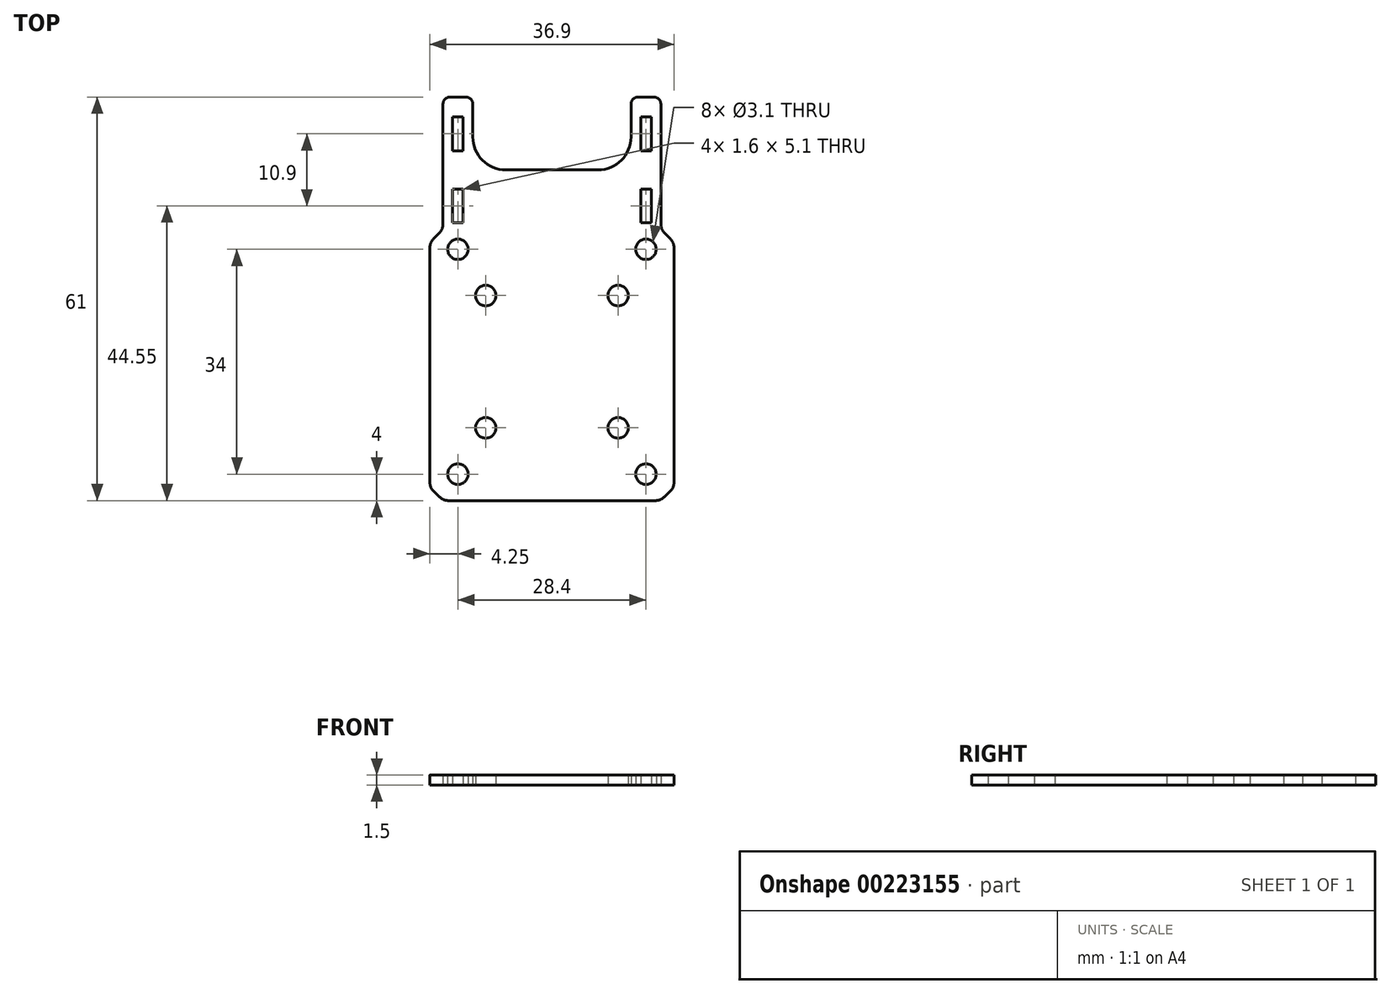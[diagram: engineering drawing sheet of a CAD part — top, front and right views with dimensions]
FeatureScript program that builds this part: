
annotation { "Feature Type Name" : "Feature", "Feature Type Description" : "" }
export const myFeature = defineFeature(function(context is Context, id is Id, definition is map)
    precondition{}
    {
        {
            var Q0;
            Q0=qCreatedBy(makeId("Top.planeOp"),FACE);
            var sketch = newSketch(context, id + "F0", { "sketchPlane" : qUnion([Q0])});
            skLineSegment(sketch, "E0.bottom", {"start": v(16.45, -30.5) * mm, "end": v(-16.45, -30.5) * mm});
            skLineSegment(sketch, "E0.left", {"start": v(16.45, -30.5) * mm, "end": v(16.45, 30.5) * mm});
            skLineSegment(sketch, "E0.right", {"start": v(-16.45, -30.5) * mm, "end": v(-16.45, 30.5) * mm});
            skPoint(sketch, "E0.middle", {"position": v(0, 0) * mm});
            skLineSegment(sketch, "E1.bottom", {"start": v(-15, 27.5) * mm, "end": v(-13.4, 27.5) * mm});
            skLineSegment(sketch, "E1.top", {"start": v(-15, 22.4) * mm, "end": v(-13.4, 22.4) * mm});
            skLineSegment(sketch, "E1.left", {"start": v(-15, 27.5) * mm, "end": v(-15, 22.4) * mm});
            skLineSegment(sketch, "E1.right", {"start": v(-13.4, 27.5) * mm, "end": v(-13.4, 22.4) * mm});
            skLineSegment(sketch, "E2.bottom", {"start": v(15, 27.5) * mm, "end": v(13.4, 27.5) * mm});
            skLineSegment(sketch, "E2.top", {"start": v(15, 22.4) * mm, "end": v(13.4, 22.4) * mm});
            skLineSegment(sketch, "E2.left", {"start": v(15, 27.5) * mm, "end": v(15, 22.4) * mm});
            skLineSegment(sketch, "E2.right", {"start": v(13.4, 27.5) * mm, "end": v(13.4, 22.4) * mm});
            skLineSegment(sketch, "E3.bottom", {"start": v(-15, 16.6) * mm, "end": v(-13.4, 16.6) * mm});
            skLineSegment(sketch, "E3.top", {"start": v(-15, 11.5) * mm, "end": v(-13.4, 11.5) * mm});
            skLineSegment(sketch, "E3.left", {"start": v(-15, 16.6) * mm, "end": v(-15, 11.5) * mm});
            skLineSegment(sketch, "E3.right", {"start": v(-13.4, 16.6) * mm, "end": v(-13.4, 11.5) * mm});
            skLineSegment(sketch, "E4.bottom", {"start": v(13.4, 16.6) * mm, "end": v(15, 16.6) * mm});
            skLineSegment(sketch, "E4.top", {"start": v(13.4, 11.5) * mm, "end": v(15, 11.5) * mm});
            skLineSegment(sketch, "E4.left", {"start": v(13.4, 16.6) * mm, "end": v(13.4, 11.5) * mm});
            skLineSegment(sketch, "E4.right", {"start": v(15, 16.6) * mm, "end": v(15, 11.5) * mm});
            skCircle(sketch, "E5", {"center": v(-10, 0.5) * mm, "radius": 1.55 * mm});
            skCircle(sketch, "E6", {"center": v(10, 0.5) * mm, "radius": 1.55 * mm});
            skCircle(sketch, "E7", {"center": v(10, -19.5) * mm, "radius": 1.55 * mm});
            skCircle(sketch, "E8", {"center": v(-10, -19.5) * mm, "radius": 1.55 * mm});
            skCircle(sketch, "E9", {"center": v(14.2, 7.5) * mm, "radius": 1.55 * mm});
            skPoint(sketch, "E9.centerSnap0", {"position": v(14.2, 11.5) * mm});
            skCircle(sketch, "E10", {"center": v(-14.2, 7.5) * mm, "radius": 1.55 * mm});
            skPoint(sketch, "E10.centerSnap0", {"position": v(-14.2, 11.5) * mm});
            skLineSegment(sketch, "E11", {"start": v(-16.45, 30.5) * mm, "end": v(-11.95, 30.5) * mm});
            skLineSegment(sketch, "E12", {"start": v(-11.95, 30.5) * mm, "end": v(-11.95, 19.5) * mm});
            skLineSegment(sketch, "E13", {"start": v(-11.95, 19.5) * mm, "end": v(11.95, 19.5) * mm});
            skLineSegment(sketch, "E14", {"start": v(11.95, 19.5) * mm, "end": v(11.95, 30.5) * mm});
            skLineSegment(sketch, "E15", {"start": v(11.95, 30.5) * mm, "end": v(16.45, 30.5) * mm});
            skCircle(sketch, "E16", {"center": v(14.2, -26.5) * mm, "radius": 1.55 * mm});
            skCircle(sketch, "E17", {"center": v(-14.2, -26.5) * mm, "radius": 1.55 * mm});
            skLineSegment(sketch, "E18.bottom", {"start": v(16.45, 10.5) * mm, "end": v(18.45, 8.5) * mm});
            skLineSegment(sketch, "E18.top", {"start": v(16.45, -30.5) * mm, "end": v(18.45, -28.5) * mm});
            skLineSegment(sketch, "E18.left", {"start": v(16.45, 10.5) * mm, "end": v(16.45, -30.5) * mm});
            skLineSegment(sketch, "E18.right", {"start": v(18.45, 8.5) * mm, "end": v(18.45, -28.5) * mm});
            skLineSegment(sketch, "E19.bottom", {"start": v(-16.45, 10.5) * mm, "end": v(-18.45, 8.5) * mm});
            skLineSegment(sketch, "E19.top", {"start": v(-16.45, -30.5) * mm, "end": v(-18.45, -28.5) * mm});
            skLineSegment(sketch, "E19.left", {"start": v(-16.45, 10.5) * mm, "end": v(-16.45, -30.5) * mm});
            skLineSegment(sketch, "E19.right", {"start": v(-18.45, 8.5) * mm, "end": v(-18.45, -28.5) * mm});
            skSolve(sketch);
        }
        {
            var Q0;
            Q0 = qSketchRegion(id + "F0", true);
            extrude(context, id + "F1", {"entities" : qUnion([Q0]), "depth" : 1.5 * mm});
        }
        {
            var Q0;
            Q0=makeQuery(id+"F1.opExtrude","SWEPT_EDGE",EDGE,{"disambiguationData":[OSD([sQuery(id+"F0.wireOp",EDGE,"E12"),sQuery(id+"F0.wireOp",EDGE,"E13")])]});
            var Q1;
            Q1=makeQuery(id+"F1.opExtrude","SWEPT_EDGE",EDGE,{"disambiguationData":[OSD([sQuery(id+"F0.wireOp",EDGE,"E13"),sQuery(id+"F0.wireOp",EDGE,"E14")])]});
            fillet(context, id + "F2", {"entities" : qUnion([Q0, Q1]), "radius" : 5 * mm, "tangentPropagation" : true, "allowEdgeOverflow" : false});
        }
        {
            var Q0;
            Q0=makeQuery(id+"F1.opExtrude","SWEPT_EDGE",EDGE,{"disambiguationData":[OSD([sQuery(id+"F0.wireOp",EDGE,"E0.left"),sQuery(id+"F0.wireOp",EDGE,"E18.top"),sQuery(id+"F0.wireOp",EDGE,"E18.left")])]});
            var Q1;
            Q1=makeQuery(id+"F1.opExtrude","SWEPT_EDGE",EDGE,{"disambiguationData":[OSD([sQuery(id+"F0.wireOp",EDGE,"E18.top"),sQuery(id+"F0.wireOp",EDGE,"E18.right")])]});
            var Q2;
            Q2=makeQuery(id+"F1.opExtrude","SWEPT_EDGE",EDGE,{"disambiguationData":[OSD([sQuery(id+"F0.wireOp",EDGE,"E19.top"),sQuery(id+"F0.wireOp",EDGE,"E19.right")])]});
            var Q3;
            Q3=makeQuery(id+"F1.opExtrude","SWEPT_EDGE",EDGE,{"disambiguationData":[OSD([sQuery(id+"F0.wireOp",EDGE,"E0.right"),sQuery(id+"F0.wireOp",EDGE,"E19.top"),sQuery(id+"F0.wireOp",EDGE,"E19.left")])]});
            var Q4;
            Q4=makeQuery(id+"F1.opExtrude","SWEPT_EDGE",EDGE,{"disambiguationData":[OSD([sQuery(id+"F0.wireOp",EDGE,"E19.bottom"),sQuery(id+"F0.wireOp",EDGE,"E19.right")])]});
            var Q5;
            Q5=makeQuery(id+"F1.opExtrude","SWEPT_EDGE",EDGE,{"disambiguationData":[OSD([sQuery(id+"F0.wireOp",EDGE,"E0.right"),sQuery(id+"F0.wireOp",EDGE,"E19.bottom"),sQuery(id+"F0.wireOp",EDGE,"E19.left")])]});
            var Q6;
            Q6=makeQuery(id+"F1.opExtrude","SWEPT_EDGE",EDGE,{"disambiguationData":[OSD([sQuery(id+"F0.wireOp",EDGE,"E0.left"),sQuery(id+"F0.wireOp",EDGE,"E18.bottom"),sQuery(id+"F0.wireOp",EDGE,"E18.left")])]});
            var Q7;
            Q7=makeQuery(id+"F1.opExtrude","SWEPT_EDGE",EDGE,{"disambiguationData":[OSD([sQuery(id+"F0.wireOp",EDGE,"E18.bottom"),sQuery(id+"F0.wireOp",EDGE,"E18.right")])]});
            fillet(context, id + "F3", {"entities" : qUnion([Q0, Q1, Q2, Q3, Q4, Q5, Q6, Q7]), "radius" : 2 * mm, "tangentPropagation" : true, "allowEdgeOverflow" : false});
        }
        {
            var Q0;
            Q0=makeQuery(id+"F1.opExtrude","SWEPT_EDGE",EDGE,{"disambiguationData":[OSD([sQuery(id+"F0.wireOp",EDGE,"E0.left"),sQuery(id+"F0.wireOp",EDGE,"E15")])]});
            var Q1;
            Q1=makeQuery(id+"F1.opExtrude","SWEPT_EDGE",EDGE,{"disambiguationData":[OSD([sQuery(id+"F0.wireOp",EDGE,"E14"),sQuery(id+"F0.wireOp",EDGE,"E15")])]});
            var Q2;
            Q2=makeQuery(id+"F1.opExtrude","SWEPT_EDGE",EDGE,{"disambiguationData":[OSD([sQuery(id+"F0.wireOp",EDGE,"E11"),sQuery(id+"F0.wireOp",EDGE,"E12")])]});
            var Q3;
            Q3=makeQuery(id+"F1.opExtrude","SWEPT_EDGE",EDGE,{"disambiguationData":[OSD([sQuery(id+"F0.wireOp",EDGE,"E0.right"),sQuery(id+"F0.wireOp",EDGE,"E11")])]});
            fillet(context, id + "F4", {"entities" : qUnion([Q0, Q1, Q2, Q3]), "radius" : 1 * mm, "tangentPropagation" : true, "allowEdgeOverflow" : false});
        }
    });
